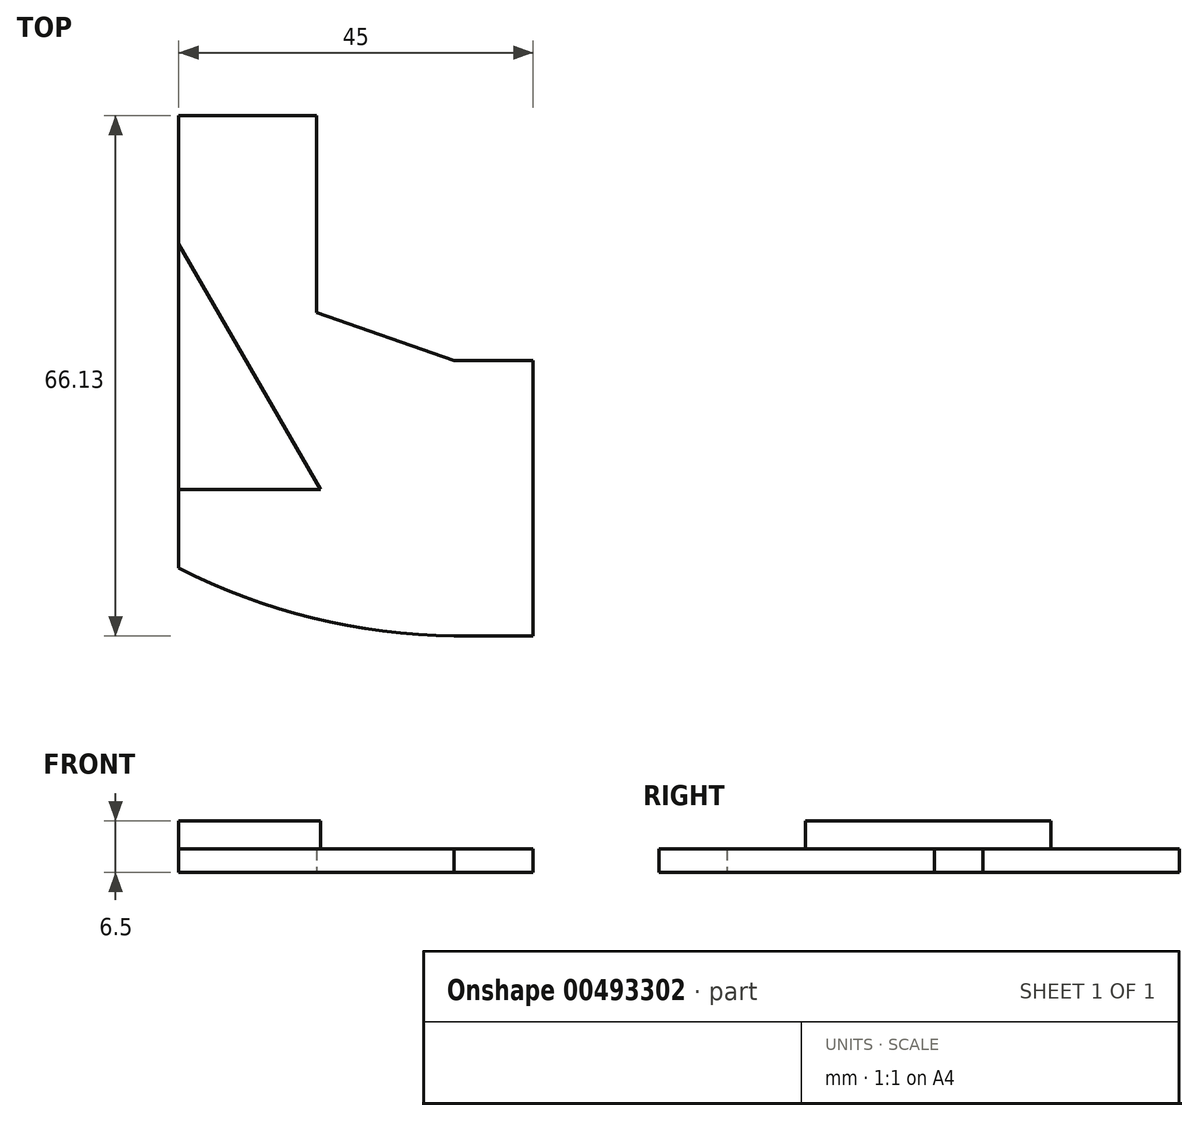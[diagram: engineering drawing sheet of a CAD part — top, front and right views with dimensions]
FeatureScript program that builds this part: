
annotation { "Feature Type Name" : "Feature", "Feature Type Description" : "" }
export const myFeature = defineFeature(function(context is Context, id is Id, definition is map)
    precondition{}
    {
        {
            var Q0;
            Q0=qCreatedBy(makeId("Top.planeOp"),FACE);
            var sketch = newSketch(context, id + "F0", { "sketchPlane" : qUnion([Q0])});
            skLineSegment(sketch, "E0", {"start": v(-35, 31.13) * mm, "end": v(-35, -26.37) * mm});
            skLineSegment(sketch, "E1", {"start": v(-35, 31.13) * mm, "end": v(-17.5, 31.13) * mm});
            skLineSegment(sketch, "E2", {"start": v(-17.5, 31.13) * mm, "end": v(-17.5, 6.13) * mm});
            skLineSegment(sketch, "E3", {"start": v(0, 0) * mm, "end": v(10, 0) * mm});
            skLineSegment(sketch, "E4", {"start": v(10, 0) * mm, "end": v(10, -35) * mm});
            skArc(sketch, "E5", {"start": v(0, -35) * mm, "mid": v(-18, -32.68) * mm, "end": v(-35, -26.37) * mm});
            skLineSegment(sketch, "E6", {"start": v(10, -35) * mm, "end": v(0, -35) * mm});
            skLineSegment(sketch, "E7", {"start": v(-17.5, 6.13) * mm, "end": v(0, 0) * mm});
            skSolve(sketch);
        }
        {
            var Q0;
            Q0=makeQuery(id+"F0.imprint","IMPRINT",FACE,{"disambiguationData":[TD([[makeQuery(id+"F0.imprint","IMPRINT",EDGE,{"derivedFrom":sQuery(id+"F0.wireOp",EDGE,"E0")}),1.0]])]});
            extrude(context, id + "F1", {"entities" : qUnion([Q0]), "depth" : 3 * mm});
        }
        {
            var Q0;
            Q0=makeQuery(id+"F1.opExtrude","CAP_FACE",FACE,{"disambiguationData":[OSD([sQuery(id+"F0.wireOp",EDGE,"E0"),sQuery(id+"F0.wireOp",EDGE,"E1"),sQuery(id+"F0.wireOp",EDGE,"E2"),sQuery(id+"F0.wireOp",EDGE,"E3"),sQuery(id+"F0.wireOp",EDGE,"E4"),sQuery(id+"F0.wireOp",EDGE,"E5"),sQuery(id+"F0.wireOp",EDGE,"E6"),sQuery(id+"F0.wireOp",EDGE,"E7")])],"isStart":false});
            var sketch = newSketch(context, id + "F2", { "sketchPlane" : qUnion([Q0])});
            skLineSegment(sketch, "E8", {"start": v(-35, -16.37) * mm, "end": v(-17, -16.37) * mm});
            skLineSegment(sketch, "E9", {"start": v(-17, -16.37) * mm, "end": v(-35, 14.8) * mm});
            skLineSegment(sketch, "E10", {"start": v(-35, 14.8) * mm, "end": v(-35, -16.37) * mm});
            skSolve(sketch);
        }
        {
            var Q0;
            Q0=makeQuery(id+"F2.imprint","IMPRINT",FACE,{"disambiguationData":[TD([[makeQuery(id+"F2.imprint","IMPRINT",EDGE,{"derivedFrom":sQuery(id+"F2.wireOp",EDGE,"E8")}),1.0]])]});
            extrude(context, id + "F3", {"entities" : qUnion([Q0]), "operationType" : NewBodyOperationType.ADD, "depth" : 3.5 * mm});
        }
    });
